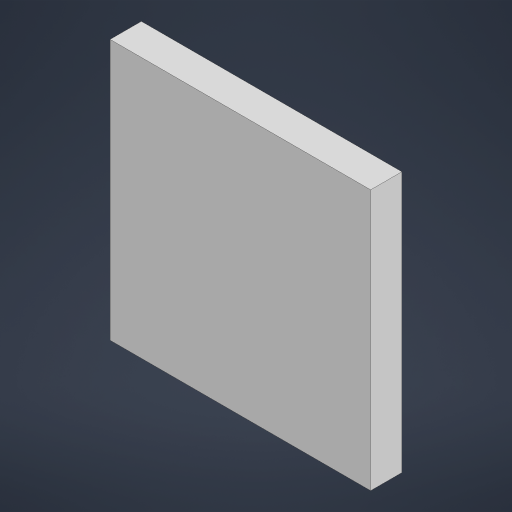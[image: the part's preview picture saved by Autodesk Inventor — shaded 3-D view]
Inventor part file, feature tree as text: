
AUTODESK INVENTOR PART (.ipt)
format: ipt  version: 2024.2 (Build 282272000, 272)  size: 397,824 bytes
history: native  units: mm
features: other x4, extrude x2, sketch x2, reference x2
ambient origin geometry x8: Origin, YZ Plane, XZ Plane, XY Plane, X Axis, Y Axis, Z Axis, Center Point
bodies: Body1 (feature_tree)
feature tree (10):
  other  "솔리드1"
  extrude  "돌출1"  Depth=2.0mm
  extrude  "돌출2"  Depth=5.0mm TaperAngle=0.0deg
  sketch  "스케치1"
  reference  "참조1"
  sketch  "스케치2"
  reference  "참조2"
  other  "<userpath>\Downloads\AAST\PART\AAST Remote Controler\apple logo light module.iam"
  other  "apple logo light module.iam"
  other  "light balance panel:1"
